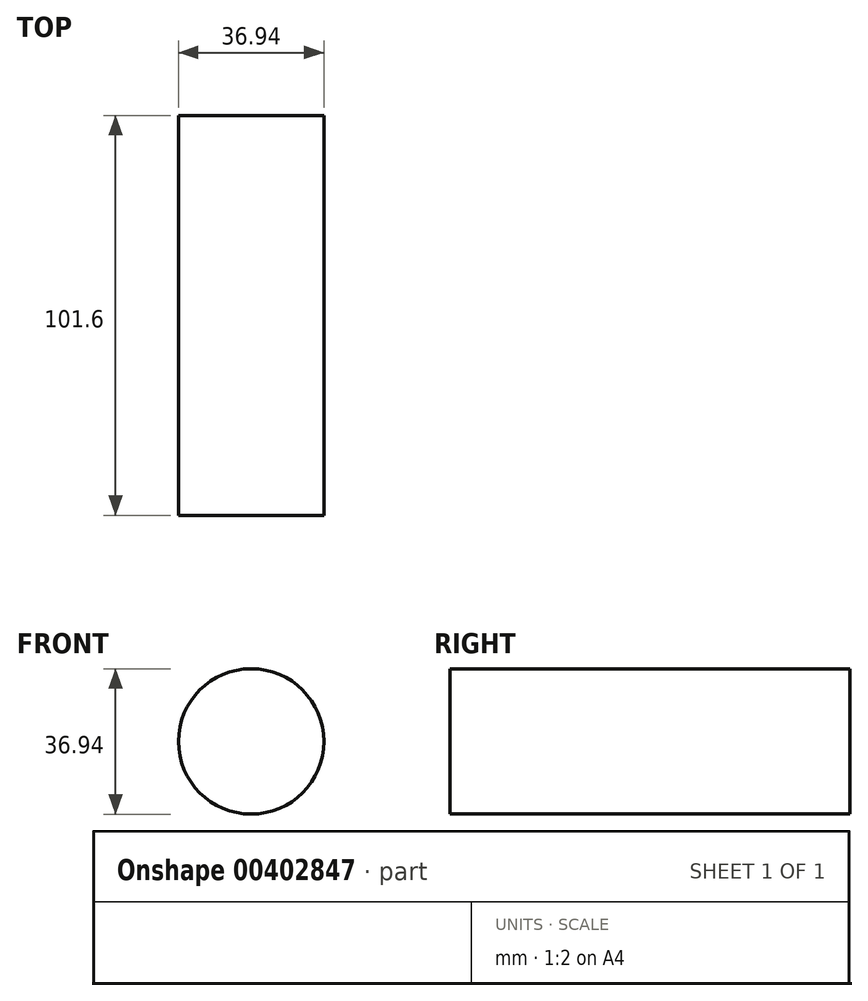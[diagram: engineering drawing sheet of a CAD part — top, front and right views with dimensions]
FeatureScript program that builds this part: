
annotation { "Feature Type Name" : "Feature", "Feature Type Description" : "" }
export const myFeature = defineFeature(function(context is Context, id is Id, definition is map)
    precondition{}
    {
        {
            var Q0;
            Q0=qCreatedBy(makeId("Front.planeOp"),FACE);
            var sketch = newSketch(context, id + "F0", { "sketchPlane" : qUnion([Q0])});
            skCircle(sketch, "E0", {"center": v(0, 0) * mm, "radius": 18.47 * mm});
            skSolve(sketch);
        }
        {
            var Q0;
            Q0 = qSketchRegion(id + "F0", true);
            var Q1;
            Q1=makeQuery(id+"F0.imprint","IMPRINT",FACE,{"disambiguationData":[TD([[makeQuery(id+"F0.imprint","IMPRINT",EDGE,{"derivedFrom":sQuery(id+"F0.wireOp",EDGE,"E0")}),1.0]])]});
            extrude(context, id + "F1", {"entities" : qUnion([Q0, Q1]), "depth" : 101.6 * mm});
        }
    });
